# Revit family: naughtone_NOPUL_PullmanBooth
name_source: partatom
category: Furniture
revit_build: Autodesk Revit 2018 (Build: 20170223_1515(x64)
units: mm (PartAtom-declared; Revit-internal decimal feet)

## family parameters
Always vertical = Yes
Cut with Voids When Loaded = No
OmniClass Number = 23.40.20.00
OmniClass Title = General Furniture and Specialties
Room Calculation Point = No
Shared = Yes
Work Plane-Based = No

## types (1)
- Pullman 2 Seat Booth
    AccessibilityPerformance = Table Top
    Assembly Code = E2020200
    AssetType = Movable
    BIMObjectName = NAU_Naughtone_Seating_Pullman
    Category = Pr_40_50_31 : Furniture booths
    Color = Various
    CushionOffset = 1.1 "
    Description = Pullman 2 Seat Booth
    DurationUnit = year
    Finish = Fabric upholstery
    HasLargeTable = No
    HasSmallTable = No
    IfcExportAs = IfcFurnishingElementType
    IfcExportType = BOOTH
    MainColor = Various
    Manufacturer = naughtone
    ManufacturerAddress = Knaresborough Tech Park, Manse Lane, Knaresborough, HG5 8LF
    ManufacturerName = Naughtone
    ManufacturerURL = www.naughtone.com
    Material = Fabric, plywood frame, foam, steel/wooden legs, wooden table top
    Model = NOPUL2
    ModelNumber = PULB2H
    ModelReference = Pullman 2 Seat Booth
    NBSDescription = Seating
    NBSReference = 45-35-72/352
    Name = Seating_Pullman_Naughtone
    NominalHeight = 51.181 "
    NominalLength = 51.181 "
    NominalWidth = 87.85 "
    NumberOfChairs = 4
    Package Qty = 1
    Product Description = http://www.naughtone.com
    ProductInformation = www.naughtone.com/products/pullman/
    Revision = 1
    Shape = Rectangular
    Size = 1950 x 1300 x 1300mm
    SustainabilityPerformance = FSC certifeied, SCS indoor advantage gold
    URL = www.naughtone.com
    Uniclass2015Code = Pr_40_50_31
    Uniclass2015Title = Furniture booths
    Version = 1
    WarrantyDescription = Request warranty information from naughtone
    WarrantyDurationLabor = 7
    WarrantyDurationParts = 7
    WarrantyDurationUnit = year
    WorksurfaceArea = 0 m²

## geometry (parser evidence)
native form markers: Sweep x3
no freeform markers — native parametric forms only
